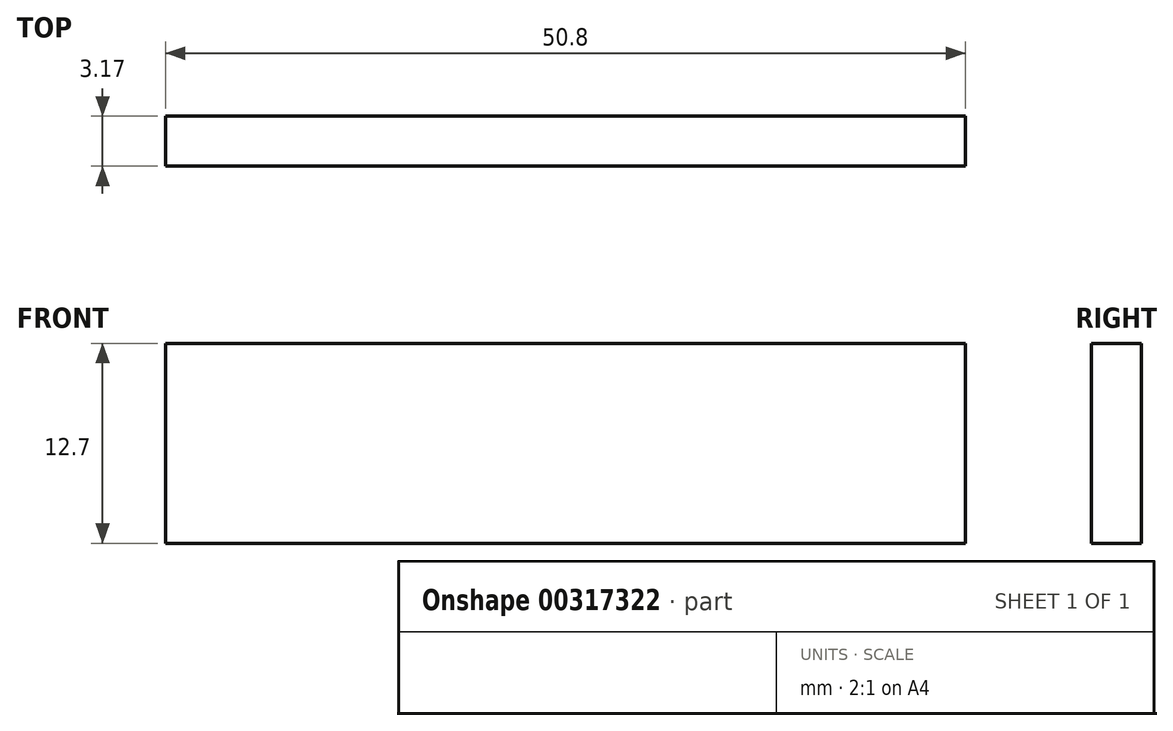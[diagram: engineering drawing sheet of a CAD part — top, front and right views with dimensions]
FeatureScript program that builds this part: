
annotation { "Feature Type Name" : "Feature", "Feature Type Description" : "" }
export const myFeature = defineFeature(function(context is Context, id is Id, definition is map)
    precondition{}
    {
        {
            var Q0;
            Q0=qCreatedBy(makeId("Front.planeOp"),FACE);
            var sketch = newSketch(context, id + "F0", { "sketchPlane" : qUnion([Q0])});
            skLineSegment(sketch, "E0.bottom", {"start": v(25.4, 6.35) * mm, "end": v(-25.4, 6.35) * mm});
            skLineSegment(sketch, "E0.top", {"start": v(25.4, -6.35) * mm, "end": v(-25.4, -6.35) * mm});
            skLineSegment(sketch, "E0.left", {"start": v(25.4, 6.35) * mm, "end": v(25.4, -6.35) * mm});
            skLineSegment(sketch, "E0.right", {"start": v(-25.4, 6.35) * mm, "end": v(-25.4, -6.35) * mm});
            skPoint(sketch, "E0.middle", {"position": v(0, 0) * mm});
            skSolve(sketch);
        }
        {
            var Q0;
            Q0 = qSketchRegion(id + "F0", true);
            extrude(context, id + "F1", {"entities" : qUnion([Q0]), "depth" : 3.17 * mm});
        }
    });
